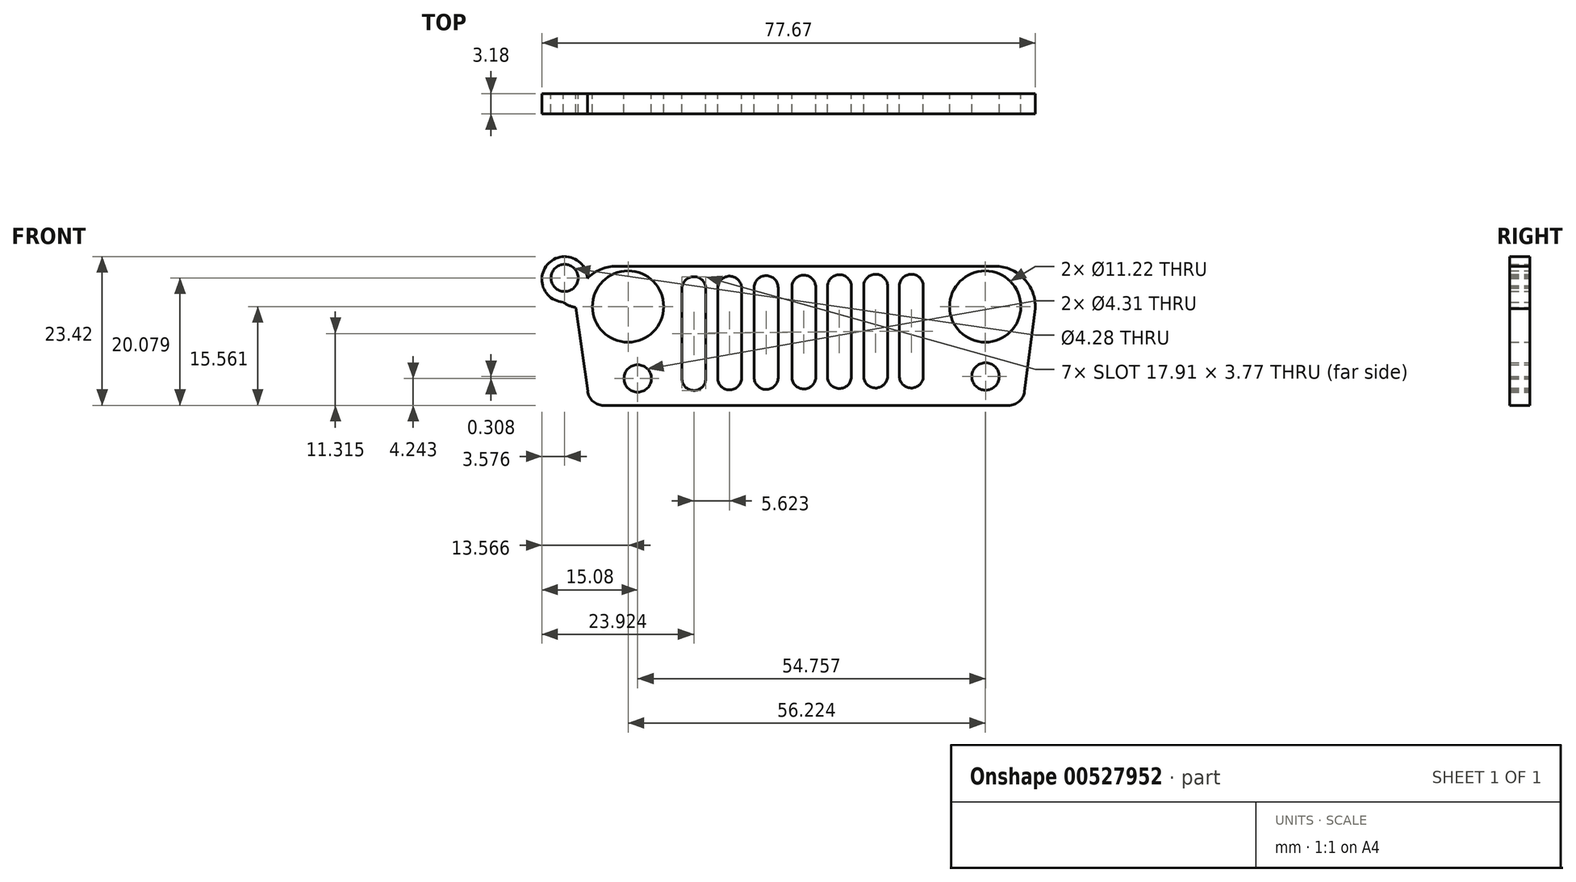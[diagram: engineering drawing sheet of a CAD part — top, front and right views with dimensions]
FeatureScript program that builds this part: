
annotation { "Feature Type Name" : "Feature", "Feature Type Description" : "" }
export const myFeature = defineFeature(function(context is Context, id is Id, definition is map)
    precondition{}
    {
        {
            var Q0;
            Q0=qCreatedBy(makeId("Front.planeOp"),FACE);
            var sketch = newSketch(context, id + "F0", { "sketchPlane" : qUnion([Q0])});
            skLineSegment(sketch, "E0.bottom", {"start": v(-40.14, 38.3) * mm, "end": v(19.48, 38.3) * mm});
            skLineSegment(sketch, "E0.top", {"start": v(-42.11, 16.4) * mm, "end": v(21.62, 16.4) * mm});
            skArc(sketch, "E1.filletArc", {"start": v(-40.14, 38.3) * mm, "mid": v(-44.69, 36.39) * mm, "end": v(-46.5, 31.8) * mm});
            skPoint(sketch, "E2.visualSharp", {"position": v(30.06, 38.3) * mm});
            skArc(sketch, "E2.filletArc", {"start": v(25.82, 31.64) * mm, "mid": v(24.08, 36.33) * mm, "end": v(19.48, 38.3) * mm});
            skLineSegment(sketch, "E3", {"start": v(-46.5, 31.8) * mm, "end": v(-44.63, 18.58) * mm});
            skLineSegment(sketch, "E4", {"start": v(25.82, 31.64) * mm, "end": v(24.14, 18.6) * mm});
            skArc(sketch, "E5.filletArc", {"start": v(-44.63, 18.58) * mm, "mid": v(-43.78, 17.02) * mm, "end": v(-42.11, 16.4) * mm});
            skArc(sketch, "E6.filletArc", {"start": v(21.62, 16.4) * mm, "mid": v(23.3, 17.03) * mm, "end": v(24.14, 18.6) * mm});
            skPoint(sketch, "E7.visualSharp", {"position": v(-46.5, 31.8) * mm});
            skCircle(sketch, "E8", {"center": v(-38.27, 31.95) * mm, "radius": 5.6 * mm});
            skArc(sketch, "E9", {"start": v(-25.78, 20.56) * mm, "mid": v(-25.77, 20.5) * mm, "end": v(-25.75, 20.45) * mm});
            skLineSegment(sketch, "E10", {"start": v(-29.8, 34.85) * mm, "end": v(-29.8, 20.56) * mm});
            skLineSegment(sketch, "E11", {"start": v(-26.03, 20.56) * mm, "end": v(-26.03, 34.78) * mm});
            skArc(sketch, "E12", {"start": v(-26.03, 34.78) * mm, "mid": v(-27.88, 36.66) * mm, "end": v(-29.8, 34.85) * mm});
            skArc(sketch, "E13", {"start": v(-29.8, 20.63) * mm, "mid": v(-27.95, 18.75) * mm, "end": v(-26.03, 20.56) * mm});
            skLineSegment(sketch, "E14", {"start": v(-24.18, 34.93) * mm, "end": v(-24.18, 20.63) * mm});
            skLineSegment(sketch, "E15", {"start": v(-20.4, 20.63) * mm, "end": v(-20.4, 34.85) * mm});
            skArc(sketch, "E16", {"start": v(-20.4, 34.85) * mm, "mid": v(-22.26, 36.74) * mm, "end": v(-24.18, 34.93) * mm});
            skArc(sketch, "E17", {"start": v(-24.18, 20.7) * mm, "mid": v(-22.33, 18.83) * mm, "end": v(-20.4, 20.63) * mm});
            skLineSegment(sketch, "E18", {"start": v(-18.42, 35) * mm, "end": v(-18.42, 20.7) * mm});
            skLineSegment(sketch, "E19", {"start": v(-14.65, 20.7) * mm, "end": v(-14.65, 34.93) * mm});
            skArc(sketch, "E20", {"start": v(-14.65, 34.93) * mm, "mid": v(-16.5, 36.81) * mm, "end": v(-18.42, 35) * mm});
            skArc(sketch, "E21", {"start": v(-18.42, 20.79) * mm, "mid": v(-16.57, 18.9) * mm, "end": v(-14.65, 20.7) * mm});
            skLineSegment(sketch, "E22", {"start": v(-12.5, 35.08) * mm, "end": v(-12.5, 20.79) * mm});
            skLineSegment(sketch, "E23", {"start": v(-8.73, 20.79) * mm, "end": v(-8.73, 35) * mm});
            skArc(sketch, "E24", {"start": v(-8.73, 35) * mm, "mid": v(-10.57, 36.9) * mm, "end": v(-12.5, 35.08) * mm});
            skArc(sketch, "E25", {"start": v(-12.5, 20.86) * mm, "mid": v(-10.65, 18.98) * mm, "end": v(-8.73, 20.79) * mm});
            skLineSegment(sketch, "E26", {"start": v(-6.89, 35.16) * mm, "end": v(-6.89, 20.86) * mm});
            skLineSegment(sketch, "E27", {"start": v(-3.12, 20.86) * mm, "end": v(-3.12, 35.08) * mm});
            skArc(sketch, "E28", {"start": v(-3.12, 35.08) * mm, "mid": v(-4.97, 36.97) * mm, "end": v(-6.89, 35.16) * mm});
            skArc(sketch, "E29", {"start": v(-6.89, 20.94) * mm, "mid": v(-5.04, 19.06) * mm, "end": v(-3.12, 20.86) * mm});
            skLineSegment(sketch, "E30", {"start": v(-1.19, 35.24) * mm, "end": v(-1.19, 20.94) * mm});
            skLineSegment(sketch, "E31", {"start": v(2.58, 20.94) * mm, "end": v(2.58, 35.16) * mm});
            skArc(sketch, "E32", {"start": v(2.58, 35.16) * mm, "mid": v(0.73, 37.05) * mm, "end": v(-1.19, 35.24) * mm});
            skArc(sketch, "E33", {"start": v(-1.19, 21.02) * mm, "mid": v(0.66, 19.13) * mm, "end": v(2.58, 20.94) * mm});
            skLineSegment(sketch, "E34", {"start": v(4.43, 35.24) * mm, "end": v(4.43, 20.94) * mm});
            skLineSegment(sketch, "E35", {"start": v(8.2, 20.94) * mm, "end": v(8.2, 35.16) * mm});
            skArc(sketch, "E36", {"start": v(8.2, 35.16) * mm, "mid": v(6.35, 37.05) * mm, "end": v(4.43, 35.24) * mm});
            skArc(sketch, "E37", {"start": v(4.43, 21.02) * mm, "mid": v(6.28, 19.13) * mm, "end": v(8.2, 20.94) * mm});
            skCircle(sketch, "E38", {"center": v(17.95, 31.95) * mm, "radius": 5.6 * mm});
            skCircle(sketch, "E39", {"center": v(18, 20.94) * mm, "radius": 2.16 * mm});
            skCircle(sketch, "E40", {"center": v(-36.76, 20.63) * mm, "radius": 2.16 * mm});
            skArc(sketch, "E41", {"start": v(-48.48, 32.65) * mm, "mid": v(-47.54, 32.1) * mm, "end": v(-46.5, 31.8) * mm});
            skArc(sketch, "E42", {"start": v(-44.69, 36.39) * mm, "mid": v(-50.78, 38.78) * mm, "end": v(-48.48, 32.65) * mm});
            skCircle(sketch, "E43", {"center": v(-48.26, 36.47) * mm, "radius": 2.14 * mm});
            skSolve(sketch);
        }
        {
            var Q0;
            Q0=makeQuery(id+"F0.imprint","IMPRINT",FACE,{"disambiguationData":[TD([[makeQuery(id+"F0.imprint","IMPRINT",EDGE,{"derivedFrom":sQuery(id+"F0.wireOp",EDGE,"E0.bottom")}),-1.0]])]});
            extrude(context, id + "F1", {"entities" : qUnion([Q0]), "depth" : 3.17 * mm, "offsetDistance" : 25.4 * mm});
        }
        {
            var Q0;
            Q0 = qSketchRegion(id + "F0", true);
            extrude(context, id + "F2", {"entities" : qUnion([Q0]), "operationType" : NewBodyOperationType.ADD, "depth" : 1 / 203.2 * mm, "offsetDistance" : 25.4 * mm});
        }
        {
            var Q0;
            Q0 = qSketchRegion(id + "F0", true);
            extrude(context, id + "F3", {"entities" : qUnion([Q0]), "operationType" : NewBodyOperationType.ADD, "depth" : 3.17 * mm, "offsetDistance" : 25.4 * mm});
        }
    });
